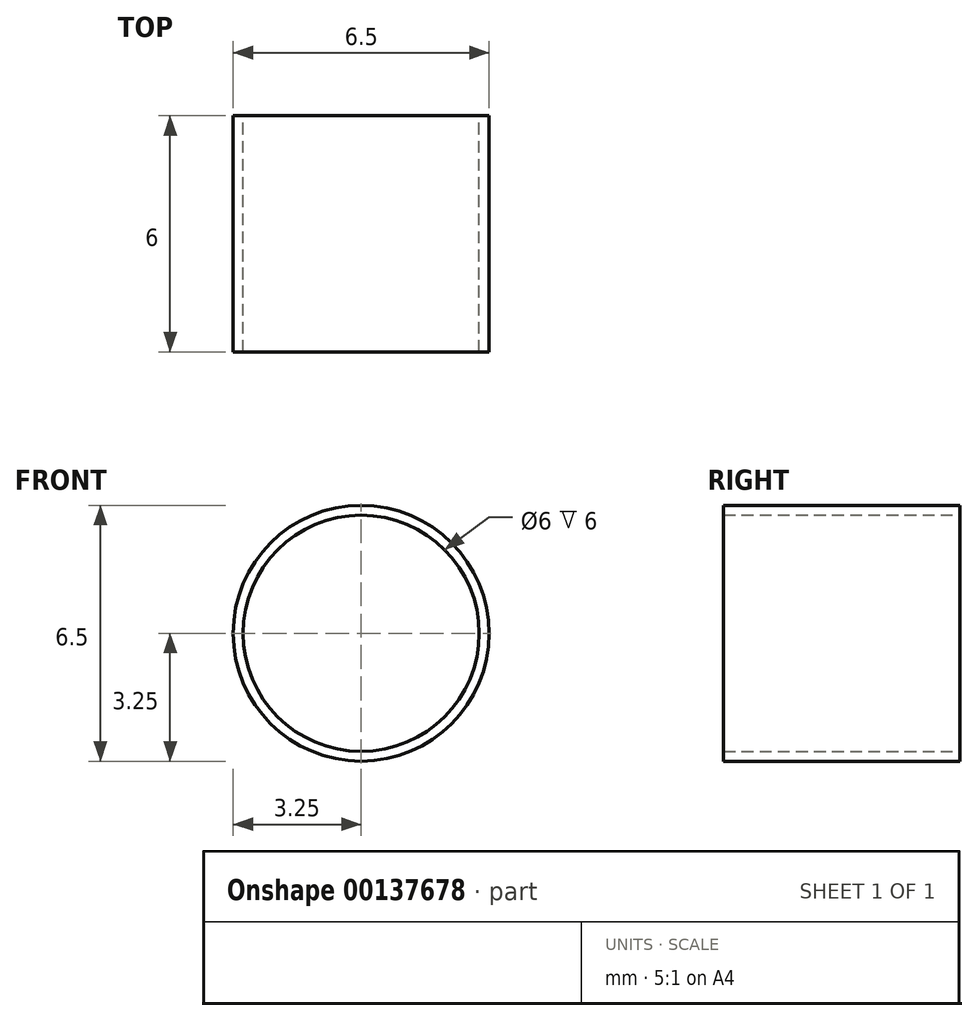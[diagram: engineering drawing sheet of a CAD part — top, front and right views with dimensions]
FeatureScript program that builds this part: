
annotation { "Feature Type Name" : "Feature", "Feature Type Description" : "" }
export const myFeature = defineFeature(function(context is Context, id is Id, definition is map)
    precondition{}
    {
        {
            var Q0;
            Q0=qCreatedBy(makeId("Front.planeOp"),FACE);
            var sketch = newSketch(context, id + "F0", { "sketchPlane" : qUnion([Q0])});
            skCircle(sketch, "E0", {"center": v(0, 0) * mm, "radius": 3 * mm});
            skCircle(sketch, "E1", {"center": v(0, 0) * mm, "radius": 3.25 * mm});
            skSolve(sketch);
        }
        {
            var Q0;
            Q0 = qSketchRegion(id + "F0", true);
            extrude(context, id + "F1", {"entities" : qUnion([Q0]), "depth" : 6 * mm});
        }
    });
